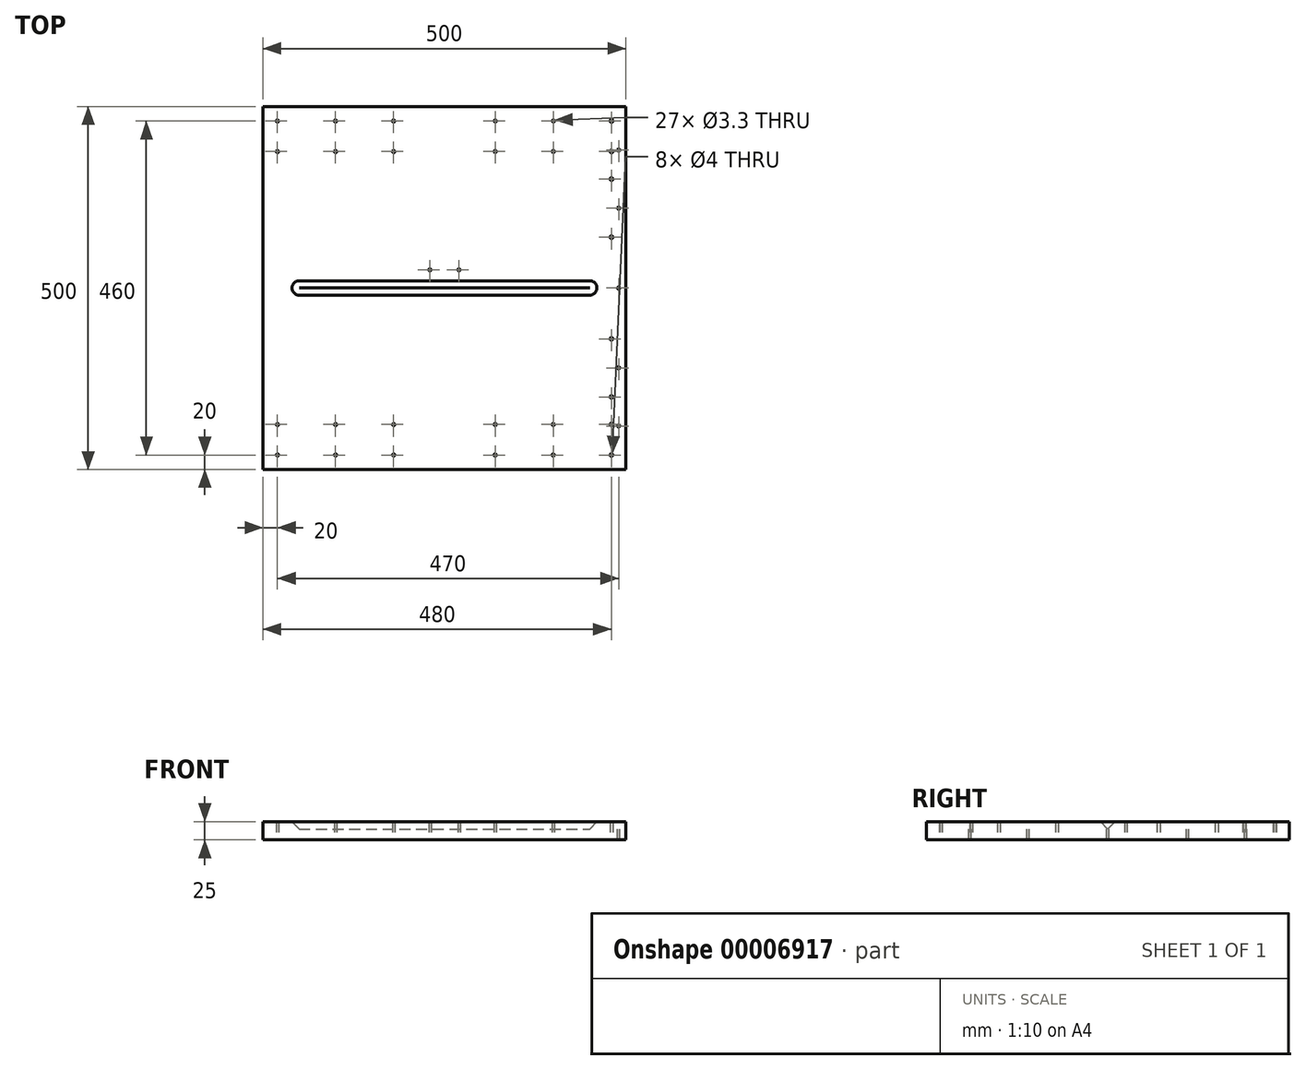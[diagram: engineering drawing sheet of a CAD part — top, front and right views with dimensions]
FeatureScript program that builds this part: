
annotation { "Feature Type Name" : "Feature", "Feature Type Description" : "" }
export const myFeature = defineFeature(function(context is Context, id is Id, definition is map)
    precondition{}
    {
        {
            var Q0;
            Q0=qCreatedBy(makeId("Top.planeOp"),FACE);
            var sketch = newSketch(context, id + "F0", { "sketchPlane" : qUnion([Q0])});
            skLineSegment(sketch, "E0.rect.bottom", {"start": v(250, -250) * mm, "end": v(-250, -250) * mm});
            skLineSegment(sketch, "E0.rect.top", {"start": v(250, 250) * mm, "end": v(-250, 250) * mm});
            skLineSegment(sketch, "E0.rect.left", {"start": v(250, -250) * mm, "end": v(250, 250) * mm});
            skLineSegment(sketch, "E0.rect.right", {"start": v(-250, -250) * mm, "end": v(-250, 250) * mm});
            skPoint(sketch, "E0.rect.middle", {"position": v(0, 0) * mm});
            skCircle(sketch, "E1", {"center": v(-230, 230) * mm, "radius": 1.65 * mm});
            skCircle(sketch, "E2", {"center": v(-230, 188) * mm, "radius": 1.65 * mm});
            skCircle(sketch, "E3", {"center": v(-230, -230) * mm, "radius": 1.65 * mm});
            skCircle(sketch, "E4", {"center": v(-230, -188) * mm, "radius": 1.65 * mm});
            skCircle(sketch, "E5", {"center": v(230, 188) * mm, "radius": 2 * mm});
            skCircle(sketch, "E6", {"center": v(230, 230) * mm, "radius": 2 * mm});
            skCircle(sketch, "E7", {"center": v(150, -188) * mm, "radius": 1.65 * mm});
            skCircle(sketch, "E8", {"center": v(150, -230) * mm, "radius": 1.65 * mm});
            skLineSegment(sketch, "E9", {"start": v(-250, 0) * mm, "end": v(250, 0) * mm, "construction": true});
            skLineSegment(sketch, "E10", {"start": v(0, 250) * mm, "end": v(0, -250) * mm, "construction": true});
            skCircle(sketch, "E11", {"center": v(-150, -230) * mm, "radius": 1.65 * mm});
            skCircle(sketch, "E12", {"center": v(-150, -188) * mm, "radius": 1.65 * mm});
            skCircle(sketch, "E13", {"center": v(-70, -230) * mm, "radius": 1.65 * mm});
            skCircle(sketch, "E14", {"center": v(-70, -188) * mm, "radius": 1.65 * mm});
            skCircle(sketch, "E15", {"center": v(-150, 230) * mm, "radius": 1.65 * mm});
            skCircle(sketch, "E16", {"center": v(-150, 188) * mm, "radius": 1.65 * mm});
            skCircle(sketch, "E17", {"center": v(-70, 230) * mm, "radius": 1.65 * mm});
            skCircle(sketch, "E18", {"center": v(-70, 188) * mm, "radius": 1.65 * mm});
            skCircle(sketch, "E19", {"center": v(150, 188) * mm, "radius": 1.65 * mm});
            skCircle(sketch, "E20", {"center": v(150, 230) * mm, "radius": 1.65 * mm});
            skCircle(sketch, "E21", {"center": v(70, 230) * mm, "radius": 1.65 * mm});
            skCircle(sketch, "E22", {"center": v(70, 188) * mm, "radius": 1.65 * mm});
            skCircle(sketch, "E23", {"center": v(230, -230) * mm, "radius": 2 * mm});
            skCircle(sketch, "E24", {"center": v(230, -188) * mm, "radius": 2 * mm});
            skCircle(sketch, "E25", {"center": v(70, -230) * mm, "radius": 1.65 * mm});
            skCircle(sketch, "E26", {"center": v(70, -188) * mm, "radius": 1.65 * mm});
            skCircle(sketch, "E27", {"center": v(230, -150) * mm, "radius": 2 * mm});
            skCircle(sketch, "E28", {"center": v(230, -70) * mm, "radius": 2 * mm});
            skCircle(sketch, "E29", {"center": v(230, 150) * mm, "radius": 2 * mm});
            skCircle(sketch, "E30", {"center": v(230, 70) * mm, "radius": 2 * mm});
            skCircle(sketch, "E31", {"center": v(20, 25) * mm, "radius": 1.65 * mm});
            skCircle(sketch, "E32", {"center": v(-20, 25) * mm, "radius": 1.65 * mm});
            skSolve(sketch);
        }
        {
            var Q0;
            Q0=makeQuery(id+"F0.imprint","IMPRINT",FACE,{"disambiguationData":[TD([[makeQuery(id+"F0.imprint","IMPRINT",EDGE,{"derivedFrom":sQuery(id+"F0.wireOp",EDGE,"E0.rect.bottom")}),-1.0]])]});
            extrude(context, id + "F1", {"entities" : qUnion([Q0]), "depth" : 25 * mm});
        }
        {
            var Q0;
            Q0=makeQuery(id+"F1.opExtrude","SWEPT_FACE",FACE,{"disambiguationData":[OSD([sQuery(id+"F0.wireOp",EDGE,"E0.rect.left")])]});
            var sketch = newSketch(context, id + "F2", { "sketchPlane" : qUnion([Q0])});
            skLineSegment(sketch, "E33", {"start": v(0, 0) * mm, "end": v(0, 25) * mm, "construction": true});
            skLineSegment(sketch, "E34", {"start": v(0, 15) * mm, "end": v(10, 25) * mm});
            skLineSegment(sketch, "E35", {"start": v(0, 15) * mm, "end": v(-10, 25) * mm});
            skLineSegment(sketch, "E36", {"start": v(0, 25) * mm, "end": v(10, 25) * mm});
            skLineSegment(sketch, "E37", {"start": v(0, 25) * mm, "end": v(-10, 25) * mm});
            skSolve(sketch);
        }
        {
            var Q0;
            Q0 = qSketchRegion(id + "F2", true);
            var Q1;
            {var subQ2=sQuery(id+"F2.wireOp",EDGE,"E34");Q1=makeQuery(id+"F2.imprint","IMPRINT",FACE,{"disambiguationData":[TD([[makeQuery(id+"F2.imprint","IMPRINT",EDGE,{"derivedFrom":subQ2}),1.0]])]});}
            extrude(context, id + "F3", {"entities" : qUnion([Q0, Q1]), "operationType" : NewBodyOperationType.REMOVE, "oppositeDirection" : true, "depth" : (450) * mm});
        }
        {
            var Q0;
            Q0=makeQuery(id+"F3.boolean.opBoolean","COPY",FACE,{"derivedFrom":makeQuery(id+"F3.opExtrude","CAP_FACE",FACE,{"disambiguationData":[OSD([sQuery(id+"F0.wireOp",EDGE,"E0.rect.left"),sQuery(id+"F2.wireOp",EDGE,"E34"),sQuery(id+"F2.wireOp",EDGE,"E35")])],"isStart":false})});
            var sketch = newSketch(context, id + "F4", { "sketchPlane" : qUnion([Q0])});
            skLineSegment(sketch, "E38", {"start": v(0, 15) * mm, "end": v(0, 25) * mm});
            skSolve(sketch);
        }
        {
            var Q0;
            Q0 = qSketchRegion(id + "F4", true);
            var Q1;
            {var subQ1=sQuery(id+"F4.wireOp",EDGE,"E38");Q1=makeQuery(id+"F4.imprint","IMPRINT",FACE,{"disambiguationData":[TD([[makeQuery(id+"F4.imprint","IMPRINT",EDGE,{"derivedFrom":subQ1}),-1.0]])]});}
            var Q2;
            Q2=sQuery(id+"F4.wireOp",EDGE,"E38");
            revolve(context, id + "F5", {"operationType" : NewBodyOperationType.REMOVE, "entities" : qUnion([Q0, Q1]), "axis" : qUnion([Q2]), "revolveType" : RevolveType.FULL, "oppositeDirection" : true});
        }
        {
            var Q0;
            Q0=makeQuery(id+"F1.opExtrude","SWEPT_FACE",FACE,{"disambiguationData":[OSD([sQuery(id+"F0.wireOp",EDGE,"E0.rect.left")])]});
            var sketch = newSketch(context, id + "F6", { "sketchPlane" : qUnion([Q0])});
            skLineSegment(sketch, "E39", {"start": v(-10, 25) * mm, "end": v(10, 25) * mm});
            skSolve(sketch);
        }
        {
            var Q0;
            Q0 = qSketchRegion(id + "F6", true);
            var Q1;
            Q1=makeQuery(id+"F6.imprint","IMPRINT",FACE,{"disambiguationData":[TD([[makeQuery(id+"F6.imprint","IMPRINT",EDGE,{"derivedFrom":sQuery(id+"F6.wireOp",EDGE,"E39")}),-1.0]])]});
            extrude(context, id + "F7", {"entities" : qUnion([Q0, Q1]), "oppositeDirection" : true, "depth" : (50) * mm});
        }
        {
            var Q0;
            Q0=makeQuery(id+"F1.opExtrude","SWEPT_BODY",BODY,{"disambiguationData":[OSD([sQuery(id+"F0.wireOp",EDGE,"E0.rect.bottom"),sQuery(id+"F0.wireOp",EDGE,"E0.rect.top"),sQuery(id+"F0.wireOp",EDGE,"E0.rect.left"),sQuery(id+"F0.wireOp",EDGE,"E0.rect.right"),sQuery(id+"F0.wireOp",EDGE,"E1"),sQuery(id+"F0.wireOp",EDGE,"E2"),sQuery(id+"F0.wireOp",EDGE,"E3"),sQuery(id+"F0.wireOp",EDGE,"E4"),sQuery(id+"F0.wireOp",EDGE,"E5"),sQuery(id+"F0.wireOp",EDGE,"E6"),sQuery(id+"F0.wireOp",EDGE,"E7"),sQuery(id+"F0.wireOp",EDGE,"E8"),sQuery(id+"F0.wireOp",EDGE,"5c16170e-bad2-41bf-9186-abff91bde15b"),sQuery(id+"F0.wireOp",EDGE,"b2746a3e-eb3c-457f-a3e5-932a52600d13"),sQuery(id+"F0.wireOp",EDGE,"E11"),sQuery(id+"F0.wireOp",EDGE,"E12"),sQuery(id+"F0.wireOp",EDGE,"E13"),sQuery(id+"F0.wireOp",EDGE,"E14"),sQuery(id+"F0.wireOp",EDGE,"E15"),sQuery(id+"F0.wireOp",EDGE,"E16"),sQuery(id+"F0.wireOp",EDGE,"E17"),sQuery(id+"F0.wireOp",EDGE,"E18"),sQuery(id+"F0.wireOp",EDGE,"E19"),sQuery(id+"F0.wireOp",EDGE,"E20"),sQuery(id+"F0.wireOp",EDGE,"E21"),sQuery(id+"F0.wireOp",EDGE,"E22"),sQuery(id+"F0.wireOp",EDGE,"E23"),sQuery(id+"F0.wireOp",EDGE,"E24"),sQuery(id+"F0.wireOp",EDGE,"E25"),sQuery(id+"F0.wireOp",EDGE,"E26")])]});
            var Q1;
            Q1=makeQuery(id+"F7.opExtrude","SWEPT_BODY",BODY,{"disambiguationData":[OSD([sQuery(id+"F2.wireOp",EDGE,"E34"),sQuery(id+"F2.wireOp",EDGE,"E35"),sQuery(id+"F6.wireOp",EDGE,"E39")])]});
            booleanBodies(context, id + "F8", {"operationType" : BooleanOperationType.UNION, "tools" : qUnion([Q0, Q1])});
        }
        {
            var Q0;
            Q0=makeQuery(id+"F7.opExtrude","CAP_FACE",FACE,{"disambiguationData":[OSD([sQuery(id+"F2.wireOp",EDGE,"E34"),sQuery(id+"F2.wireOp",EDGE,"E35"),sQuery(id+"F6.wireOp",EDGE,"E39")])],"isStart":false});
            var sketch = newSketch(context, id + "F9", { "sketchPlane" : qUnion([Q0])});
            skLineSegment(sketch, "E40", {"start": v(0, 15) * mm, "end": v(0, 25) * mm});
            skSolve(sketch);
        }
        {
            var Q0;
            Q0 = qSketchRegion(id + "F9", true);
            var Q1;
            {var subQ1=sQuery(id+"F9.wireOp",EDGE,"E40");Q1=makeQuery(id+"F9.imprint","IMPRINT",FACE,{"disambiguationData":[TD([[makeQuery(id+"F9.imprint","IMPRINT",EDGE,{"derivedFrom":subQ1}),-1.0]])]});}
            var Q2;
            Q2=sQuery(id+"F9.wireOp",EDGE,"E40");
            revolve(context, id + "F10", {"operationType" : NewBodyOperationType.REMOVE, "entities" : qUnion([Q0, Q1]), "axis" : qUnion([Q2]), "revolveType" : RevolveType.FULL, "oppositeDirection" : true});
        }
        {
            var Q0;
            Q0=makeQuery(id+"F8.opBoolean","MERGE",FACE,{"derivedFrom":[makeQuery(id+"F1.opExtrude","CAP_FACE",FACE,{"disambiguationData":[OSD([sQuery(id+"F0.wireOp",EDGE,"E0.rect.bottom"),sQuery(id+"F0.wireOp",EDGE,"E0.rect.top"),sQuery(id+"F0.wireOp",EDGE,"E0.rect.left"),sQuery(id+"F0.wireOp",EDGE,"E0.rect.right"),sQuery(id+"F0.wireOp",EDGE,"E1"),sQuery(id+"F0.wireOp",EDGE,"E2"),sQuery(id+"F0.wireOp",EDGE,"E3"),sQuery(id+"F0.wireOp",EDGE,"E4"),sQuery(id+"F0.wireOp",EDGE,"E5"),sQuery(id+"F0.wireOp",EDGE,"E6"),sQuery(id+"F0.wireOp",EDGE,"E7"),sQuery(id+"F0.wireOp",EDGE,"E8"),sQuery(id+"F0.wireOp",EDGE,"5c16170e-bad2-41bf-9186-abff91bde15b"),sQuery(id+"F0.wireOp",EDGE,"b2746a3e-eb3c-457f-a3e5-932a52600d13"),sQuery(id+"F0.wireOp",EDGE,"E11"),sQuery(id+"F0.wireOp",EDGE,"E12"),sQuery(id+"F0.wireOp",EDGE,"E13"),sQuery(id+"F0.wireOp",EDGE,"E14"),sQuery(id+"F0.wireOp",EDGE,"E15"),sQuery(id+"F0.wireOp",EDGE,"E16"),sQuery(id+"F0.wireOp",EDGE,"E17"),sQuery(id+"F0.wireOp",EDGE,"E18"),sQuery(id+"F0.wireOp",EDGE,"E19"),sQuery(id+"F0.wireOp",EDGE,"E20"),sQuery(id+"F0.wireOp",EDGE,"E21"),sQuery(id+"F0.wireOp",EDGE,"E22"),sQuery(id+"F0.wireOp",EDGE,"E23"),sQuery(id+"F0.wireOp",EDGE,"E24"),sQuery(id+"F0.wireOp",EDGE,"E25"),sQuery(id+"F0.wireOp",EDGE,"E26"),sQuery(id+"F0.wireOp",EDGE,"E27"),sQuery(id+"F0.wireOp",EDGE,"E28"),sQuery(id+"F0.wireOp",EDGE,"E29"),sQuery(id+"F0.wireOp",EDGE,"E30")])],"isStart":false}),makeQuery(id+"F7.opExtrude","SWEPT_FACE",FACE,{"disambiguationData":[OSD([sQuery(id+"F6.wireOp",EDGE,"E39")])]})]});
            var sketch = newSketch(context, id + "F11", { "sketchPlane" : qUnion([Q0])});
            skCircle(sketch, "E41", {"center": v(240, -190) * mm, "radius": 1.65 * mm});
            skCircle(sketch, "E42", {"center": v(240, -110) * mm, "radius": 1.65 * mm});
            skCircle(sketch, "E43", {"center": v(240, 190) * mm, "radius": 1.65 * mm});
            skCircle(sketch, "E44", {"center": v(240, 110) * mm, "radius": 1.65 * mm});
            skLineSegment(sketch, "E45", {"start": v(-250, 0) * mm, "end": v(250, 0) * mm, "construction": true});
            skCircle(sketch, "E46", {"center": v(240, 0) * mm, "radius": 1.65 * mm});
            skSolve(sketch);
        }
        {
            var Q0;
            Q0 = qSketchRegion(id + "F11", true);
            extrude(context, id + "F12", {"entities" : qUnion([Q0]), "operationType" : NewBodyOperationType.REMOVE, "endBound" : BoundingType.THROUGH_ALL, "oppositeDirection" : true, "depth" : 25 * mm});
        }
    });
